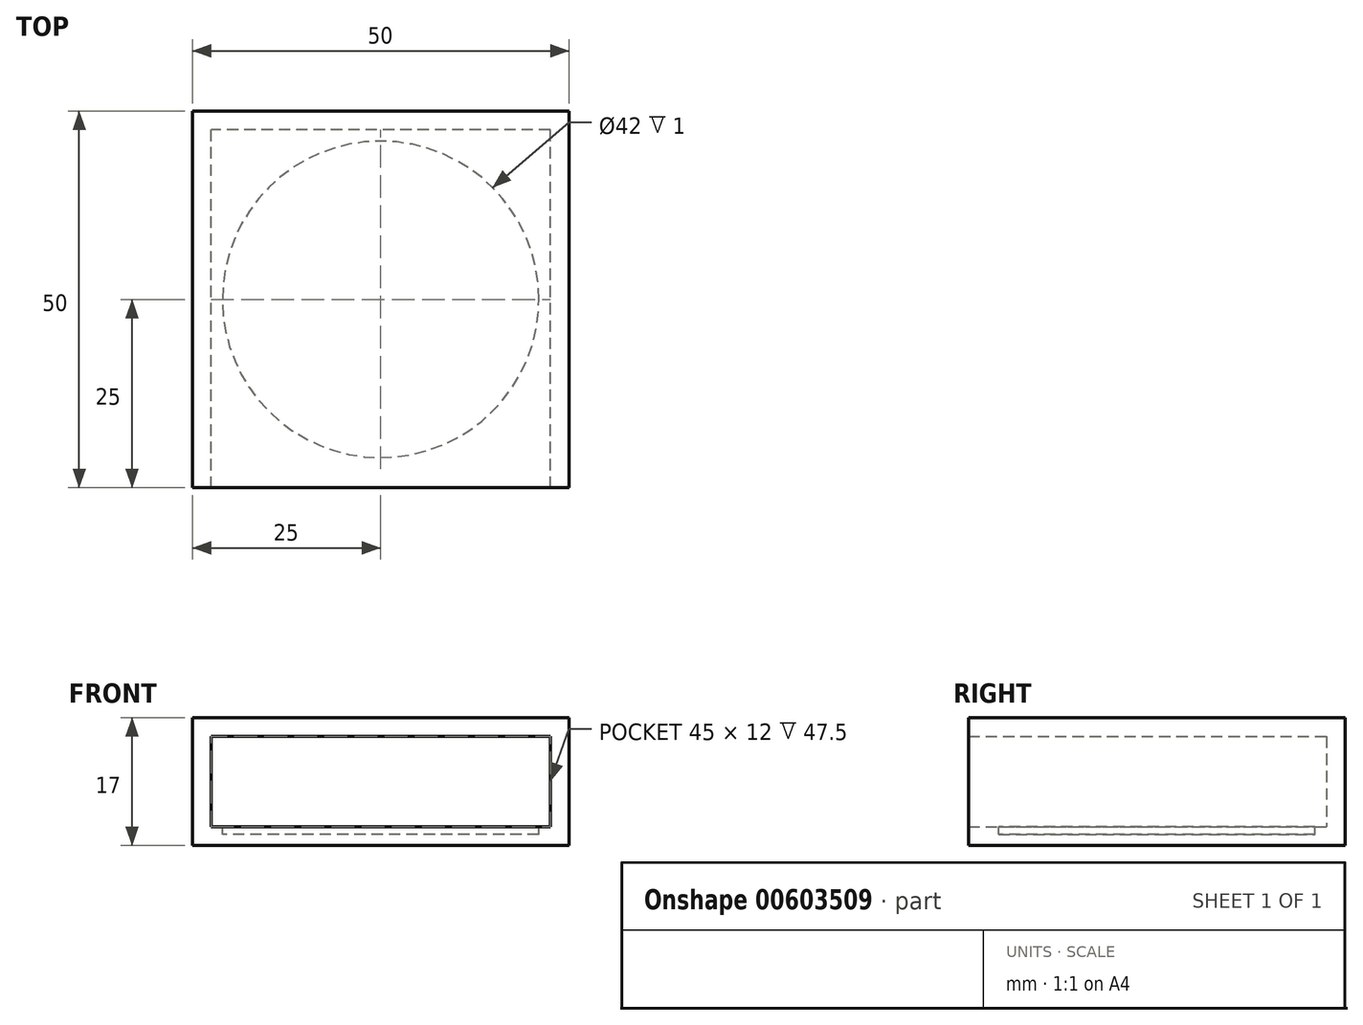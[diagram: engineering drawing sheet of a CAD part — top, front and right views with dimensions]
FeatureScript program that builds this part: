
annotation { "Feature Type Name" : "Feature", "Feature Type Description" : "" }
export const myFeature = defineFeature(function(context is Context, id is Id, definition is map)
    precondition{}
    {
        {
            var Q0;
            Q0=qCreatedBy(makeId("Top.planeOp"),FACE);
            var sketch = newSketch(context, id + "F0", { "sketchPlane" : qUnion([Q0])});
            skLineSegment(sketch, "E0.bottom", {"start": v(25, -25) * mm, "end": v(-25, -25) * mm});
            skLineSegment(sketch, "E0.top", {"start": v(25, 25) * mm, "end": v(-25, 25) * mm});
            skLineSegment(sketch, "E0.left", {"start": v(25, -25) * mm, "end": v(25, 25) * mm});
            skLineSegment(sketch, "E0.right", {"start": v(-25, -25) * mm, "end": v(-25, 25) * mm});
            skPoint(sketch, "E0.middle", {"position": v(0, 0) * mm});
            skSolve(sketch);
        }
        {
            var Q0;
            Q0=makeQuery(id+"F0.imprint","IMPRINT",FACE,{"disambiguationData":[TD([[makeQuery(id+"F0.imprint","IMPRINT",EDGE,{"derivedFrom":sQuery(id+"F0.wireOp",EDGE,"E0.bottom")}),-1.0]])]});
            extrude(context, id + "F1", {"entities" : qUnion([Q0]), "depth" : 17 * mm, "offsetDistance" : 25 * mm});
        }
        {
            var Q0;
            Q0=makeQuery(id+"F1.opExtrude","SWEPT_FACE",FACE,{"disambiguationData":[OSD([sQuery(id+"F0.wireOp",EDGE,"E0.bottom")])]});
            shell(context, id + "F2", {"entities" : qUnion([Q0]), "thickness" : 2.5 * mm});
        }
        {
            var Q0;
            {var subQ0=sQuery(id+"F0.wireOp",EDGE,"E0.right");var subQ1=sQuery(id+"F0.wireOp",EDGE,"E0.left");var subQ2=sQuery(id+"F0.wireOp",EDGE,"E0.top");var subQ3=sQuery(id+"F0.wireOp",EDGE,"E0.bottom");Q0=makeQuery(id+"F2.opShell","OFFSET_FACE",FACE,{"disambiguationData":[OSD([subQ3,subQ2,subQ1,subQ0]),TDD([makeQuery(id+"F1.opExtrude","CAP_FACE",FACE,{"disambiguationData":[OSD([subQ3,subQ2,subQ1,subQ0])],"isStart":true})])]});}
            var sketch = newSketch(context, id + "F3", { "sketchPlane" : qUnion([Q0])});
            skCircle(sketch, "E1", {"center": v(0, 0) * mm, "radius": 21 * mm});
            skSolve(sketch);
        }
        {
            var Q0;
            Q0=makeQuery(id+"F3.imprint","IMPRINT",FACE,{"disambiguationData":[TD([[makeQuery(id+"F3.imprint","IMPRINT",EDGE,{"derivedFrom":sQuery(id+"F3.wireOp",EDGE,"E1")}),1.0]])]});
            extrude(context, id + "F4", {"entities" : qUnion([Q0]), "operationType" : NewBodyOperationType.REMOVE, "oppositeDirection" : true, "depth" : 1 * mm, "offsetDistance" : 25 * mm});
        }
    });
